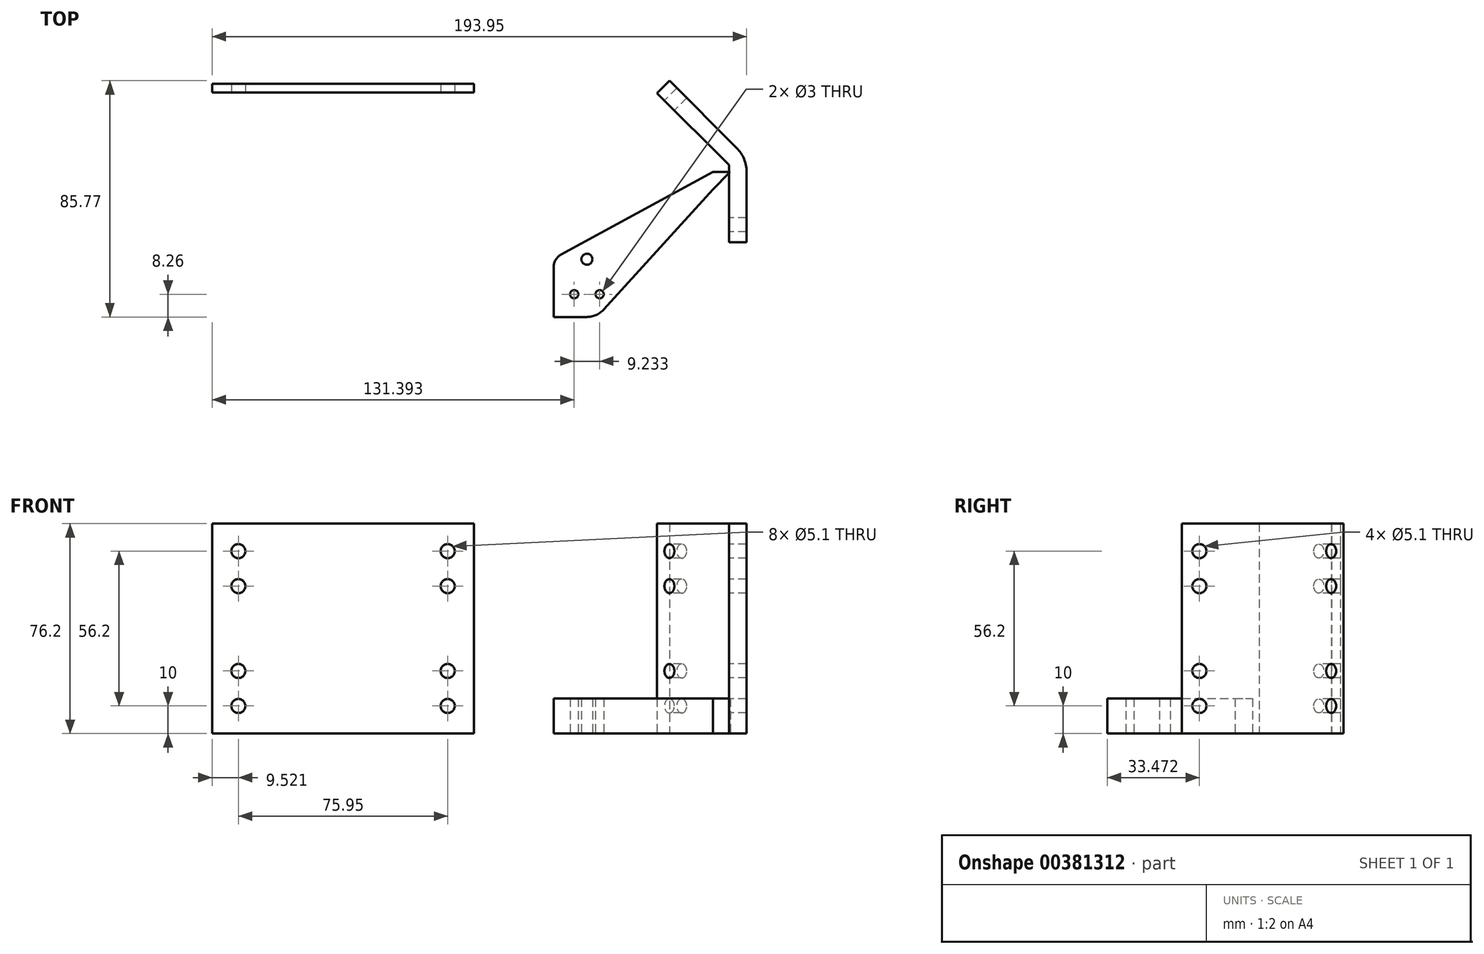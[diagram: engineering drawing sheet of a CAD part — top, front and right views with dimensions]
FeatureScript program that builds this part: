
annotation { "Feature Type Name" : "Feature", "Feature Type Description" : "" }
export const myFeature = defineFeature(function(context is Context, id is Id, definition is map)
    precondition{}
    {
        {
            var Q0;
            Q0=qCreatedBy(makeId("Top.planeOp"),FACE);
            var sketch = newSketch(context, id + "F0", { "sketchPlane" : qUnion([Q0]), "disableImprinting" : false});
            skLineSegment(sketch, "E0.bottom", {"start": v(-181.73, 31.9) * mm, "end": v(-86.73, 31.9) * mm});
            skLineSegment(sketch, "E0.top", {"start": v(-181.73, 28.72) * mm, "end": v(-86.73, 28.72) * mm});
            skLineSegment(sketch, "E0.left", {"start": v(-181.73, 31.9) * mm, "end": v(-181.73, 28.72) * mm});
            skLineSegment(sketch, "E0.right", {"start": v(-86.73, 31.9) * mm, "end": v(-86.73, 28.72) * mm});
            skLineSegment(sketch, "E1", {"start": v(4.15, 4.15) * mm, "end": v(0, 0) * mm, "construction": true});
            skLineSegment(sketch, "E2", {"start": v(5.87, 0) * mm, "end": v(0, 0) * mm, "construction": true});
            skLineSegment(sketch, "E3", {"start": v(5.87, 0) * mm, "end": v(5.87, -25.59) * mm});
            skLineSegment(sketch, "E4", {"start": v(4.15, 4.15) * mm, "end": v(-20.28, 28.57) * mm});
            skLineSegment(sketch, "E5.0", {"start": v(12.22, 0) * mm, "end": v(12.22, -25.59) * mm});
            skLineSegment(sketch, "E5.2", {"start": v(8.64, 8.64) * mm, "end": v(-15.79, 33.06) * mm});
            skLineSegment(sketch, "E6", {"start": v(-20.28, 28.57) * mm, "end": v(-15.79, 33.06) * mm});
            skLineSegment(sketch, "E7", {"start": v(5.87, -25.59) * mm, "end": v(12.22, -25.59) * mm});
            skLineSegment(sketch, "E8", {"start": v(8.64, 8.64) * mm, "end": v(4.15, 4.15) * mm, "construction": true});
            skLineSegment(sketch, "E9", {"start": v(5.87, 0) * mm, "end": v(12.22, 0) * mm, "construction": true});
            skLineSegment(sketch, "E10", {"start": v(8.64, 8.64) * mm, "end": v(8.64, 8.64) * mm});
            skLineSegment(sketch, "E11", {"start": v(12.22, 0) * mm, "end": v(12.22, 0) * mm});
            skLineSegment(sketch, "E12", {"start": v(5.87, 0) * mm, "end": v(5.87, 2.43) * mm});
            skLineSegment(sketch, "E13", {"start": v(5.87, 2.43) * mm, "end": v(4.15, 4.15) * mm});
            skPoint(sketch, "E14.0.visualSharp", {"position": v(12.22, 5.06) * mm});
            skArc(sketch, "E14.0.filletArc", {"start": v(12.22, 0) * mm, "mid": v(11.29, 4.68) * mm, "end": v(8.64, 8.64) * mm});
            skSolve(sketch);
        }
        {
            var Q0;
            Q0 = qSketchRegion(id + "F0", true);
            extrude(context, id + "F1", {"entities" : qUnion([Q0]), "depth" : 76.2 * mm});
        }
        {
            var Q0;
            Q0=makeQuery(id+"F1.opExtrude","SWEPT_FACE",FACE,{"disambiguationData":[OSD([sQuery(id+"F0.wireOp",EDGE,"E0.top")])]});
            var sketch = newSketch(context, id + "F2", { "sketchPlane" : qUnion([Q0])});
            skLineSegment(sketch, "E15", {"start": v(-181.73, 38.1) * mm, "end": v(-86.73, 38.1) * mm, "construction": true});
            skCircle(sketch, "E16", {"center": v(-96.26, 66.2) * mm, "radius": 2.55 * mm});
            skLineSegment(sketch, "E17", {"start": v(-134.23, 76.2) * mm, "end": v(-134.23, 0) * mm, "construction": true});
            skCircle(sketch, "E18.MirrorC", {"center": v(-172.2, 66.2) * mm, "radius": 2.55 * mm});
            skCircle(sketch, "E19.MirrorC", {"center": v(-96.26, 10) * mm, "radius": 2.55 * mm});
            skCircle(sketch, "E20.MirrorC", {"center": v(-172.2, 10) * mm, "radius": 2.55 * mm});
            skCircle(sketch, "E21", {"center": v(-96.26, 53.5) * mm, "radius": 2.55 * mm});
            skCircle(sketch, "E22.MirrorC", {"center": v(-96.26, 22.7) * mm, "radius": 2.55 * mm});
            skCircle(sketch, "E23.MirrorC", {"center": v(-172.2, 53.5) * mm, "radius": 2.55 * mm});
            skCircle(sketch, "E24.MirrorC", {"center": v(-172.2, 22.7) * mm, "radius": 2.55 * mm});
            skSolve(sketch);
        }
        {
            var Q0;
            Q0 = qSketchRegion(id + "F2", true);
            extrude(context, id + "F3", {"entities" : qUnion([Q0]), "operationType" : NewBodyOperationType.REMOVE, "endBound" : BoundingType.THROUGH_ALL, "oppositeDirection" : true, "depth" : 25 * mm});
        }
        {
            var Q0;
            Q0=makeQuery(id+"F1.opExtrude","SWEPT_FACE",FACE,{"disambiguationData":[OSD([sQuery(id+"F0.wireOp",EDGE,"E4")])]});
            var sketch = newSketch(context, id + "F4", { "sketchPlane" : qUnion([Q0])});
            skCircle(sketch, "E25", {"center": v(-28.2, 66.2) * mm, "radius": 2.55 * mm});
            skLineSegment(sketch, "E26", {"start": v(-34.54, 38.1) * mm, "end": v(-34.54, 38.1) * mm});
            skCircle(sketch, "E27.MirrorC", {"center": v(-28.2, 10) * mm, "radius": 2.55 * mm});
            skCircle(sketch, "E28", {"center": v(-28.2, 53.5) * mm, "radius": 2.55 * mm});
            skCircle(sketch, "E29", {"center": v(-28.2, 22.7) * mm, "radius": 2.55 * mm});
            skSolve(sketch);
        }
        {
            var Q0;
            Q0=makeQuery(id+"F1.opExtrude","SWEPT_FACE",FACE,{"disambiguationData":[OSD([sQuery(id+"F0.wireOp",EDGE,"E3")])]});
            var sketch = newSketch(context, id + "F5", { "sketchPlane" : qUnion([Q0])});
            skCircle(sketch, "E30", {"center": v(19.24, 66.2) * mm, "radius": 2.55 * mm});
            skLineSegment(sketch, "E31", {"start": v(25.59, 38.1) * mm, "end": v(25.59, 38.1) * mm});
            skCircle(sketch, "E32.MirrorC", {"center": v(19.24, 10) * mm, "radius": 2.55 * mm});
            skCircle(sketch, "E33", {"center": v(19.24, 53.5) * mm, "radius": 2.55 * mm});
            skCircle(sketch, "E34", {"center": v(19.24, 22.7) * mm, "radius": 2.55 * mm});
            skSolve(sketch);
        }
        {
            var Q0;
            Q0 = qSketchRegion(id + "F4", true);
            extrude(context, id + "F6", {"entities" : qUnion([Q0]), "operationType" : NewBodyOperationType.REMOVE, "endBound" : BoundingType.THROUGH_ALL, "oppositeDirection" : true, "offsetDistance" : 25 * mm, "depth" : 25 * mm, "hasSecondDirection" : true, "secondDirectionBound" : BoundingType.THROUGH_ALL, "secondDirectionOppositeDirection" : false, "secondDirectionDepth" : 25 * mm});
        }
        {
            var Q0;
            Q0 = qSketchRegion(id + "F5", true);
            extrude(context, id + "F7", {"entities" : qUnion([Q0]), "operationType" : NewBodyOperationType.REMOVE, "endBound" : BoundingType.THROUGH_ALL, "oppositeDirection" : true, "depth" : 25 * mm, "offsetDistance" : 25 * mm, "hasSecondDirection" : true, "secondDirectionBound" : BoundingType.THROUGH_ALL, "secondDirectionOppositeDirection" : false, "secondDirectionDepth" : 25 * mm});
        }
        {
            var Q0;
            Q0=qCreatedBy(makeId("Top.planeOp"), FACE);
            var sketch = newSketch(context, id + "F8", { "sketchPlane" : qUnion([Q0]), "disableImprinting" : false});
            skLineSegment(sketch, "E35.right", {"start": v(0, 0) * mm, "end": v(0, -6.35) * mm, "construction": true});
            skLineSegment(sketch, "E36", {"start": v(-39.6, -50) * mm, "end": v(0, -6.35) * mm});
            skCircle(sketch, "E37", {"center": v(-50.34, -44.45) * mm, "radius": 1.5 * mm});
            skCircle(sketch, "E38", {"center": v(-41.1, -44.45) * mm, "radius": 1.5 * mm});
            skCircle(sketch, "E39", {"center": v(-45.72, -31.75) * mm, "radius": 2 * mm});
            skLineSegment(sketch, "E40", {"start": v(-45.72, -31.75) * mm, "end": v(-45.72, -44.45) * mm, "construction": true});
            skLineSegment(sketch, "E41", {"start": v(-55.12, -30.09) * mm, "end": v(0, 0) * mm});
            skLineSegment(sketch, "E42", {"start": v(0, 0) * mm, "end": v(6.35, 0) * mm});
            skLineSegment(sketch, "E43", {"start": v(0, -6.35) * mm, "end": v(6.35, 0) * mm});
            skArc(sketch, "E44.0.filletArc", {"start": v(-45.72, -52.7) * mm, "mid": v(-42.38, -52) * mm, "end": v(-39.6, -50) * mm});
            skLineSegment(sketch, "E45", {"start": v(-57.76, -34.55) * mm, "end": v(-57.76, -52.7) * mm});
            skLineSegment(sketch, "E46", {"start": v(-57.76, -52.7) * mm, "end": v(-45.72, -52.7) * mm});
            skPoint(sketch, "E47.0.visualSharp", {"position": v(-57.76, -31.53) * mm});
            skArc(sketch, "E47.0.filletArc", {"start": v(-55.12, -30.09) * mm, "mid": v(-57.05, -31.95) * mm, "end": v(-57.76, -34.55) * mm});
            skSolve(sketch);
        }
        {
            var Q0;
            Q0 = qSketchRegion(id + "F8", true);
            extrude(context, id + "F9", {"entities" : qUnion([Q0]), "domain" : OperationDomain.MODEL, "flatOperationType" : FlatOperationType.REMOVE, "depth" : 12.7 * mm, "offsetDistance" : 25 * mm});
        }
    });
